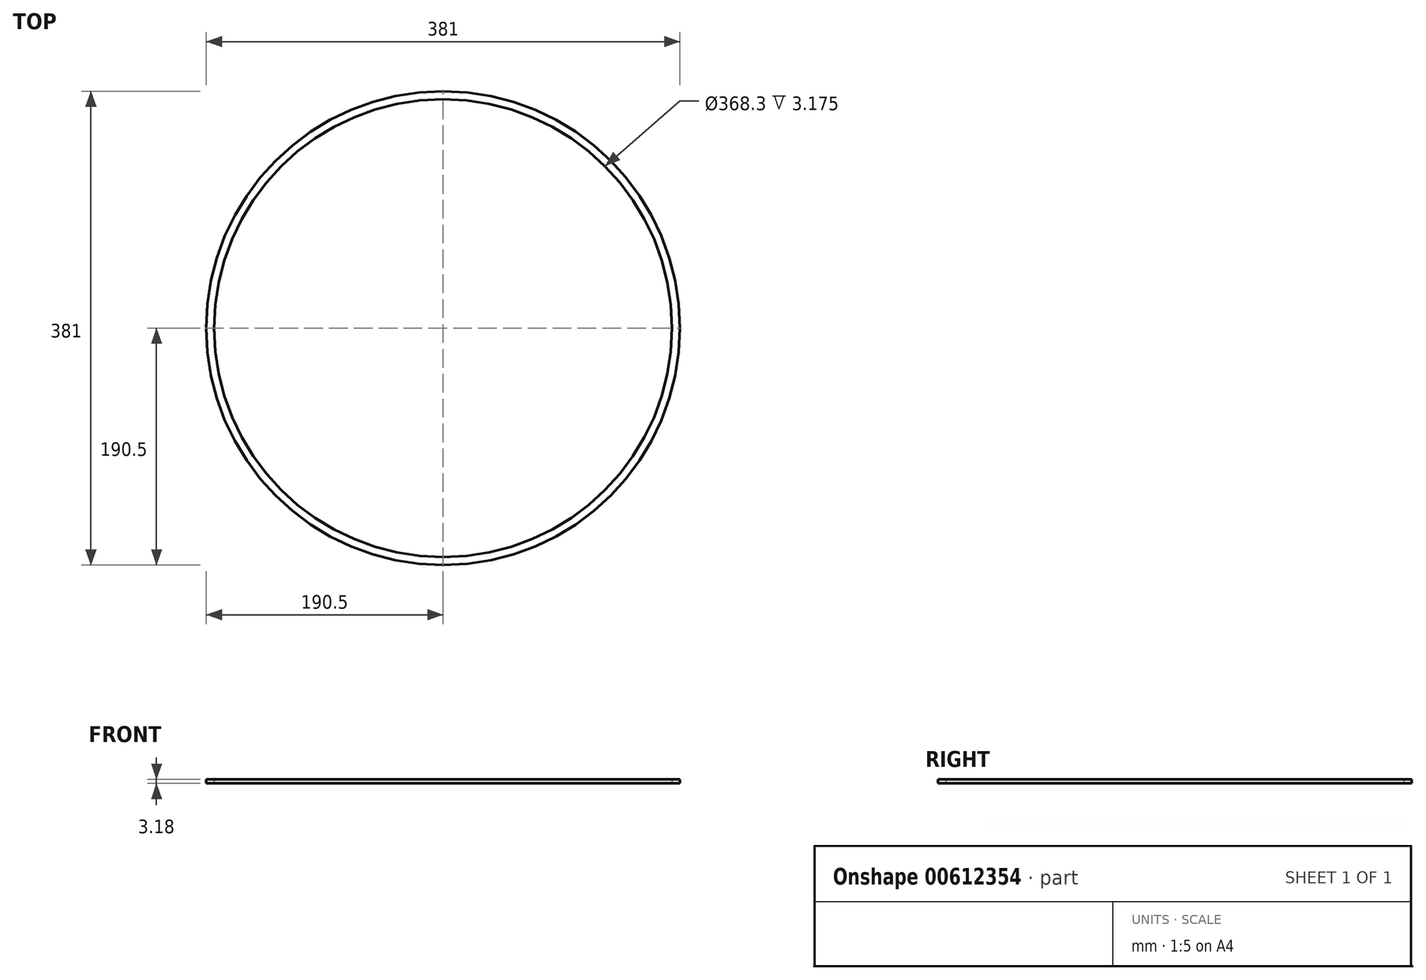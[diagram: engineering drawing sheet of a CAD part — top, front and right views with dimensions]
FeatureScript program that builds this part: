
annotation { "Feature Type Name" : "Feature", "Feature Type Description" : "" }
export const myFeature = defineFeature(function(context is Context, id is Id, definition is map)
    precondition{}
    {
        {
            var Q0;
            Q0=qCreatedBy(makeId("Front.planeOp"),FACE);
            var sketch = newSketch(context, id + "F0", { "sketchPlane" : qUnion([Q0])});
            skLineSegment(sketch, "E0", {"start": v(0, 0) * mm, "end": v(0, 131.42) * mm});
            skLineSegment(sketch, "E1.bottom", {"start": v(184.15, 0) * mm, "end": v(190.5, 0) * mm});
            skLineSegment(sketch, "E1.top", {"start": v(184.15, 3.18) * mm, "end": v(190.5, 3.18) * mm});
            skLineSegment(sketch, "E1.left", {"start": v(184.15, 0) * mm, "end": v(184.15, 3.18) * mm});
            skLineSegment(sketch, "E1.right", {"start": v(190.5, 0) * mm, "end": v(190.5, 3.18) * mm});
            skSolve(sketch);
        }
        {
            var Q0;
            Q0=makeQuery(id+"F0.imprint","IMPRINT",FACE,{"disambiguationData":[TD([[makeQuery(id+"F0.imprint","IMPRINT",EDGE,{"derivedFrom":sQuery(id+"F0.wireOp",EDGE,"E1.bottom")}),1.0]])]});
            var Q1;
            Q1=sQuery(id+"F0.wireOp",EDGE,"E0");
            revolve(context, id + "F1", {"entities" : qUnion([Q0]), "axis" : qUnion([Q1]), "revolveType" : RevolveType.FULL});
        }
    });
